# Revit family: DOVE_VIZULO
name_source: partatom
category: Lighting Fixtures
units: mm (PartAtom-declared; Revit-internal decimal feet)

## family parameters
Always vertical = Yes
Cut with Voids When Loaded = No
Light Source = Yes
OmniClass Number = 23.80.70.00
OmniClass Title = Lighting
Part Type = Normal
Room Calculation Point = No
Round Connector Dimension = Use Diameter
Shared = No
Work Plane-Based = No

## types (29) — shared parameters
Color Filter = 16777215
Dimming Lamp Color Temperature Shift = <None>
Light Source Symbol Size = 610 mm
zero-valued in all types: Default Elevation

## per-type parameters (varying)
| type | Emit from Line Length |
| 320 mm, 13 W, 3000 K | 308 mm  [stored 1.0105 ft] |
| 320 mm, 13 W, 4000 K | 308 mm  [stored 1.0105 ft] |
| 405 mm, 14 W, 3000 K | 393 mm  [stored 1.28937 ft] |
| 405 mm, 14 W, 4000 K | 393 mm  [stored 1.28937 ft] |
| 600 mm, 10 W, 3000 K | 588 mm  [stored 1.92913 ft] |
| 600 mm, 10 W, 4000 K | 588 mm  [stored 1.92913 ft] |
| 600 mm, 15 W, 3000 K | 588 mm  [stored 1.92913 ft] |
| 600 mm, 19 W, 3000 K | 588 mm  [stored 1.92913 ft] |
| 600 mm, 19 W, 4000 K | 588 mm  [stored 1.92913 ft] |
| 685 mm, 11 W, 3000 K | 673 mm  [stored 2.20801 ft] |
| 685 mm, 11 W, 4000 K | 673 mm  [stored 2.20801 ft] |
| 685 mm, 20 W, 3000 K | 673 mm  [stored 2.20801 ft] |
| 685 mm, 20 W, 4000 K | 673 mm  [stored 2.20801 ft] |
| 880 mm, 14 W, 3000 K | 868 mm  [stored 2.84777 ft] |
| 880 mm, 14 W, 4000 K | 868 mm  [stored 2.84777 ft] |
| 880 mm, 20 W, 3000 K | 868 mm  [stored 2.84777 ft] |
| 880 mm, 20 W, 4000 K | 868 mm  [stored 2.84777 ft] |
| 965 mm, 15 W, 3000 K | 953 mm  [stored 3.12664 ft] |
| 965 mm, 15 W, 4000 K | 953 mm  [stored 3.12664 ft] |
| 965 mm, 21 W, 3000 K | 953 mm  [stored 3.12664 ft] |
| 965 mm, 21 W, 4000 K | 953 mm  [stored 3.12664 ft] |
| 1160 mm, 18 W, 3000 K | 1148 mm  [stored 3.7664 ft] |
| 1160 mm, 18 W, 4000 K | 1148 mm  [stored 3.7664 ft] |
| 1160 mm, 20 W, 3000 K | 1148 mm  [stored 3.7664 ft] |
| 1160 mm, 20 W, 4000 K | 1148 mm  [stored 3.7664 ft] |
| 1245 mm, 19 W, 3000 K | 1233 mm |
| 1245 mm, 19 W, 4000 K | 1233 mm |
| 1245 mm, 21 W, 3000 K | 1233 mm |
| 1245 mm, 21 W, 4000 K | 1233 mm |

note: [stored X ft] marks values corroborated as IEEE doubles in the binary element streams (Revit-internal decimal feet)

## geometry (parser evidence)
native form markers: Sweep x3
no freeform markers — native parametric forms only
